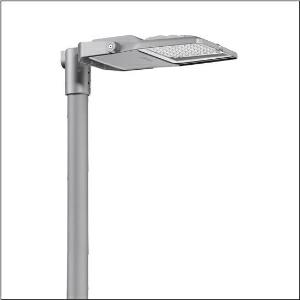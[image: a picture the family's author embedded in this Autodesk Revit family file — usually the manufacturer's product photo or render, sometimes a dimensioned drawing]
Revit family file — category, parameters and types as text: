
# Revit family: floodlight_fl_21_iq_mini___pl64_5xa7772d2e3a_5308
name_source: partatom
category: Lighting Fixtures
units: mm (PartAtom-declared; Revit-internal decimal feet)

## family parameters
Cut with Voids When Loaded = No
Host = Face
Light Source = No
Part Type = Normal
Room Calculation Point = No
Round Connector Dimension = Use Diameter
Shared = No

## types (1)
- --- (1 x LED, 17220 lm, 143 W, 3000K)
    Apparent Load = 143 VA
    CIE Flux Codes = 28 80 98 100 100
    Color Rendering = 70
    Color Temperature = 3000K
    Default Elevation = 1800 mm
    Description = Floodlight FL 21 iQ mini, floodlight, primary light control with lens, of PMMA, primary optical cover: protective disc, of toughened safety glass, transparent, light distribution: PL64, light emission: direct distribution, installation type: surface-mounted, lamps: LED, High Power LED, rated values: 17.220lm | 143W | 120,4lm/W (begin service life); end service life: 17.220lm | 151,6W; at 50% lumin. flux: 8.610lm | 60,6W | 142,1lm/W, colour temperature: 3000K, colour rendering: CRI > 70, light colour: 730, light setting 1 begin service life: 100% | 17.220lm | 143W | 120,4lm/W | 3.000K, light setting 1 end service life: 151,6W, further light settings possible, control: pre-setting: linear dimming characteristic, Auto-Match, Temp-Guard, Night-Set, Smart-Wire, Desk-Remote (wireless, voltage-free reading and setting of iQ features in the workshop via application-optimized NFC function/RFID function), optimised constant luminous flux control (CLO 2.0), Light-Fading, Lumen-Switch, with terminal, 6-pole, mains connection: 220..240V, AC, 50/60Hz, luminaire housing, of diecast aluminium, powder-coated, SITECO metallic grey (DB 702S), corrosivity category C5 mid according to DIN EN ISO 12944suitable for swimming poolschlorine-resistant, sealing non-destructively replaceable, please order mast flange separately, mast bracket, of steel, galvanised, powder-coated, protection rating (complete): IP66, insulation class (complete): insulation class II (safety insulation), certification: CE, ENEC, VDE, protection symbol: D, impact resistance: IK08, permissible operating ambient temperature: -40..+40°C, permissible operating ambient temperature for outdoor applications: -40..+50°C, standard: DIN EN 12944, LABS conformity tested according to VDMA 24364:2018-05, packaging unit: 1 piece

Light Distribution: PL64
    Height = 70 mm
    Lamp = 1 x LED
    Lamp Light Flux = 17220 lm
    Lamp Power = 143 W
    Lamp count = 1
    Length = 485 mm
    Luminous efficacy = 120 lm/W
    Manufacturer = Siteco
    ModVariant = No
    Model = 5XA7772D2E3A
    Mounting Place = Pole
    Mounting Type = Pole annexe
    Number of Poles = 1
    OnlyDefault = Yes
    Power Factor = 1
    Product Name = Floodlight FL 21 iQ mini | PL64
    Product group = floodlight | pylon annexe
    ProductGroupID = 6201
    Protection Class = Protection class II
    Protection Degree = IP 66
    RLX_Detail_Level = 1
    RLX_Emergency_Light_Flux = 0 lm
    RLX_Emergency_Type = 0
    RLX_Emergency_Type_DB = No
    RlxData = <blob elided: 101837 chars, md5=c491942b>
    Socket = socket
    Standby Power = 0 W
    System Light Flux = 17220 lm
    System Power = 143 W
    Type Comments = factory setting: luminous flux: 100 % | dim-lin: 254 | 730 mA
    Type Image = l_1007125.jpg
    URL = http://relux.com
    VarID = @adj_166835
    Voltage = 0 V
    Weight = 0.00 kg
    Width = 337 mm

## geometry (parser evidence)
native form markers: Blend x4, Sweep x12
no freeform markers — native parametric forms only
